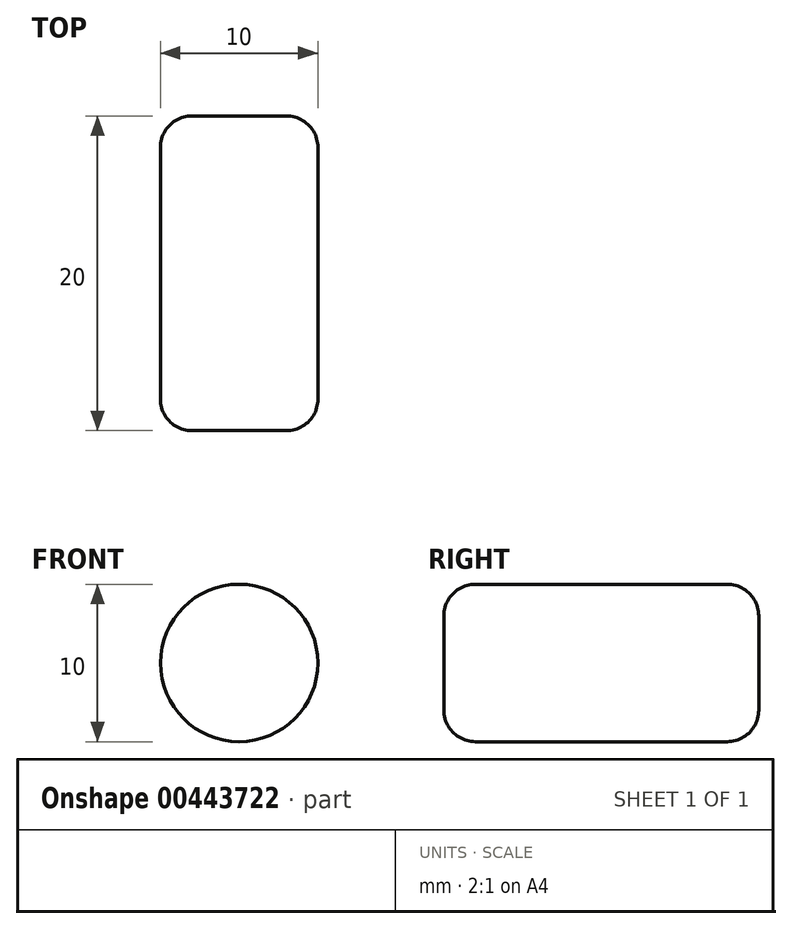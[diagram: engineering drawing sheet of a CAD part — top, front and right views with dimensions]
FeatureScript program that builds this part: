
annotation { "Feature Type Name" : "Feature", "Feature Type Description" : "" }
export const myFeature = defineFeature(function(context is Context, id is Id, definition is map)
    precondition{}
    {
        {
            var Q0;
            Q0=qCreatedBy(makeId("Front.planeOp"),FACE);
            var sketch = newSketch(context, id + "F0", { "sketchPlane" : qUnion([Q0])});
            skCircle(sketch, "E0", {"center": v(0, 0) * mm, "radius": 5 * mm});
            skSolve(sketch);
        }
        {
            var Q0;
            Q0=qSketchRegion(id+"F0",true);
            extrude(context, id + "F1", {"entities" : qUnion([Q0]), "endBound" : BoundingType.SYMMETRIC, "depth" : 20 * mm});
        }
        {
            var Q0;
            Q0=makeQuery(id+"F1.opExtrude","CAP_FACE",FACE,{"disambiguationData":[OSD([sQuery(id+"F0.wireOp",EDGE,"E0")])],"isStart":false});
            var Q1;
            Q1=makeQuery(id+"F1.opExtrude","CAP_EDGE",EDGE,{"disambiguationData":[OSD([sQuery(id+"F0.wireOp",EDGE,"E0")])],"isStart":true});
            fillet(context, id + "F2", {"entities" : qUnion([Q0, Q1]), "radius" : 2 * mm, "tangentPropagation" : true, "allowEdgeOverflow" : false});
        }
    });
